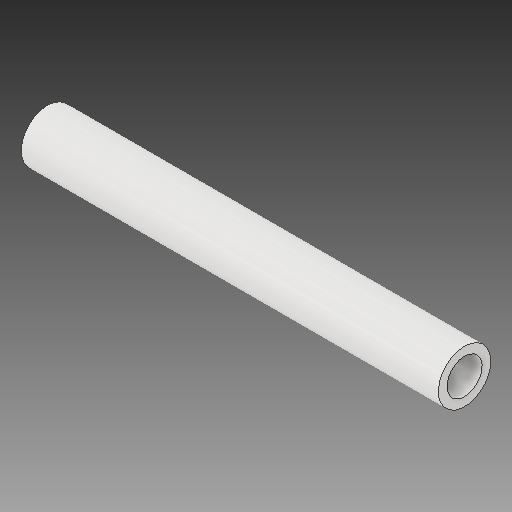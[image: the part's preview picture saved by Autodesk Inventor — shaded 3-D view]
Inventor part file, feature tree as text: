
AUTODESK INVENTOR PART (.ipt)
format: ipt  version: 2017.3 (Build 213256000, 256)  size: 92,672 bytes
history: native  units: mm
features: extrude x1, sketch x1
ambient origin geometry x8: Origin, YZ Plane, XZ Plane, XY Plane, X Axis, Y Axis, Z Axis, Center Point
bodies: Body1 (feature_tree)
feature tree (2):
  extrude  "Extrusion3"  Depth=19.0mm
  sketch  "Sketch4"  dims[d12=2.39mm d13=1.6mm d14=19.0mm d15=0.0mm]
